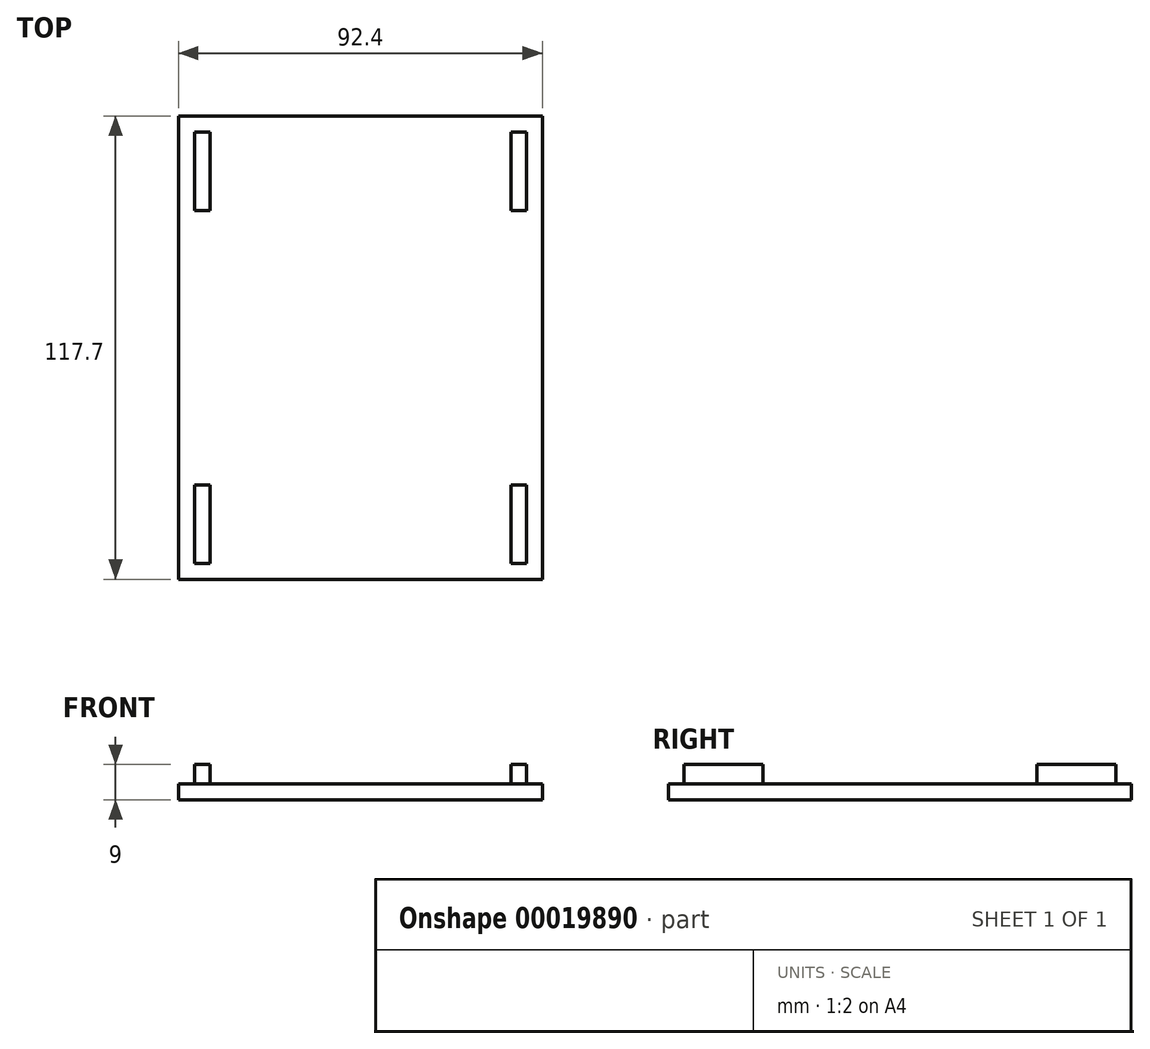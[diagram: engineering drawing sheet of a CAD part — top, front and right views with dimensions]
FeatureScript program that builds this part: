
annotation { "Feature Type Name" : "Feature", "Feature Type Description" : "" }
export const myFeature = defineFeature(function(context is Context, id is Id, definition is map)
    precondition{}
    {
        {
            var Q0;
            Q0=qCreatedBy(makeId("Top.planeOp"),FACE);
            var sketch = newSketch(context, id + "F0", { "sketchPlane" : qUnion([Q0])});
            skLineSegment(sketch, "E0.rect.bottom", {"start": v(-46.2, 58.85) * mm, "end": v(46.2, 58.85) * mm});
            skLineSegment(sketch, "E0.rect.top", {"start": v(-46.2, -58.85) * mm, "end": v(46.2, -58.85) * mm});
            skLineSegment(sketch, "E0.rect.left", {"start": v(-46.2, 58.85) * mm, "end": v(-46.2, -58.85) * mm});
            skLineSegment(sketch, "E0.rect.right", {"start": v(46.2, 58.85) * mm, "end": v(46.2, -58.85) * mm});
            skPoint(sketch, "E0.rect.middle", {"position": v(0, 0) * mm});
            skSolve(sketch);
        }
        {
            var Q0;
            Q0 = qSketchRegion(id + "F0", true);
            extrude(context, id + "F1", {"entities" : qUnion([Q0]), "depth" : 4 * mm});
        }
        {
            var Q0;
            Q0=makeQuery(id+"F1.opExtrude","CAP_FACE",FACE,{"disambiguationData":[OSD([sQuery(id+"F0.wireOp",EDGE,"E0.rect.bottom"),sQuery(id+"F0.wireOp",EDGE,"E0.rect.top"),sQuery(id+"F0.wireOp",EDGE,"E0.rect.left"),sQuery(id+"F0.wireOp",EDGE,"E0.rect.right")])],"isStart":false});
            var sketch = newSketch(context, id + "F2", { "sketchPlane" : qUnion([Q0])});
            skLineSegment(sketch, "E1.bottom", {"start": v(-42.2, 54.85) * mm, "end": v(-38.2, 54.85) * mm});
            skLineSegment(sketch, "E1.top", {"start": v(-42.2, 34.85) * mm, "end": v(-38.2, 34.85) * mm});
            skLineSegment(sketch, "E1.left", {"start": v(-42.2, 54.85) * mm, "end": v(-42.2, 34.85) * mm});
            skLineSegment(sketch, "E1.right", {"start": v(-38.2, 54.85) * mm, "end": v(-38.2, 34.85) * mm});
            skLineSegment(sketch, "E2.MirrorCS", {"start": v(42.2, 34.85) * mm, "end": v(38.2, 34.85) * mm});
            skLineSegment(sketch, "E3.MirrorCS", {"start": v(42.2, 54.85) * mm, "end": v(38.2, 54.85) * mm});
            skLineSegment(sketch, "E4.MirrorCS", {"start": v(38.2, 54.85) * mm, "end": v(38.2, 34.85) * mm});
            skLineSegment(sketch, "E5.MirrorCS", {"start": v(42.2, 54.85) * mm, "end": v(42.2, 34.85) * mm});
            skLineSegment(sketch, "E6.MirrorCS", {"start": v(-42.2, -54.85) * mm, "end": v(-38.2, -54.85) * mm});
            skLineSegment(sketch, "E7.MirrorCS", {"start": v(42.2, -54.85) * mm, "end": v(38.2, -54.85) * mm});
            skLineSegment(sketch, "E8.MirrorCS", {"start": v(42.2, -34.85) * mm, "end": v(38.2, -34.85) * mm});
            skLineSegment(sketch, "E9.MirrorCS", {"start": v(-42.2, -34.85) * mm, "end": v(-38.2, -34.85) * mm});
            skLineSegment(sketch, "E10.MirrorCS", {"start": v(38.2, -54.85) * mm, "end": v(38.2, -34.85) * mm});
            skLineSegment(sketch, "E11.MirrorCS", {"start": v(-38.2, -54.85) * mm, "end": v(-38.2, -34.85) * mm});
            skLineSegment(sketch, "E12.MirrorCS", {"start": v(-42.2, -54.85) * mm, "end": v(-42.2, -34.85) * mm});
            skLineSegment(sketch, "E13.MirrorCS", {"start": v(42.2, -54.85) * mm, "end": v(42.2, -34.85) * mm});
            skSolve(sketch);
        }
        {
            var Q0;
            Q0 = qSketchRegion(id + "F2", true);
            extrude(context, id + "F3", {"entities" : qUnion([Q0]), "operationType" : NewBodyOperationType.ADD, "depth" : 5 * mm});
        }
    });
